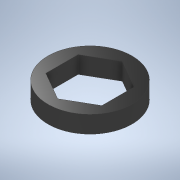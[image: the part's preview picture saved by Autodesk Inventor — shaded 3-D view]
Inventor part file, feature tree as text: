
AUTODESK INVENTOR PART (.ipt)
format: ipt  version: 2020 (Build 240168000, 168)  size: 105,984 bytes
history: native  units: in
note: dims shown in document units (in); Inventor stores cm internally (conversion verified against a paired STEP export)
features: extrude x1, sketch x1
ambient origin geometry x8: Origin, YZ Plane, XZ Plane, XY Plane, X Axis, Y Axis, Z Axis, Center Point
bodies: Solid1 (feature_tree)
feature tree (2):
  extrude  "Extrusion1"  Depth=0.5in
  sketch  "Sketch1"  dims[d0=0.75in d1=0.5in d2=0.153in d3=0.0in]
